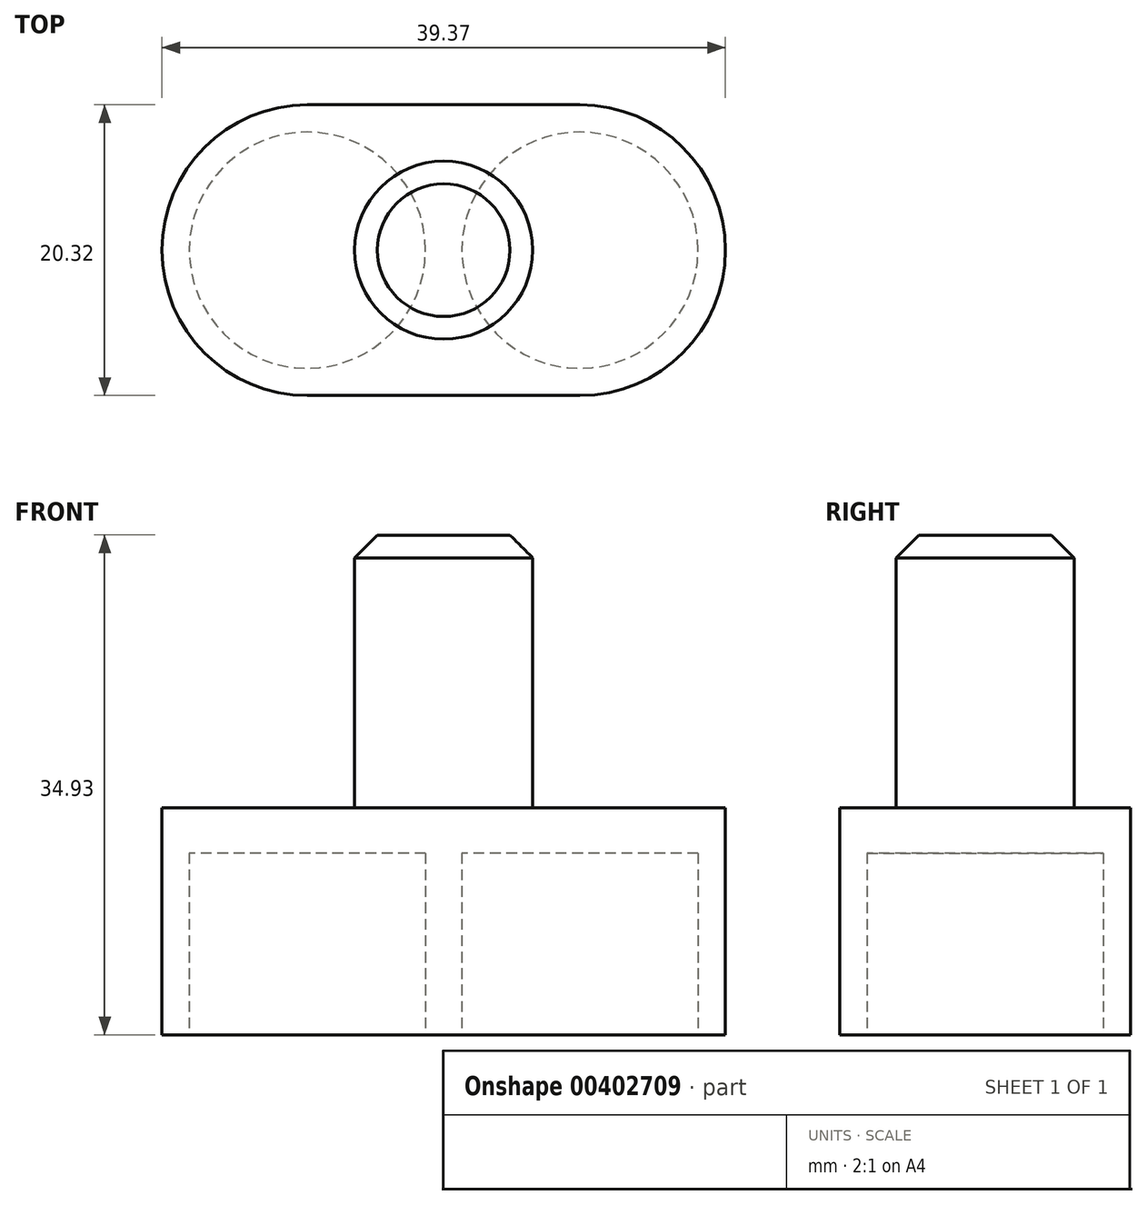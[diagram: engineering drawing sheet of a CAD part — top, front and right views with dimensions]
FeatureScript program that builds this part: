
annotation { "Feature Type Name" : "Feature", "Feature Type Description" : "" }
export const myFeature = defineFeature(function(context is Context, id is Id, definition is map)
    precondition{}
    {
        {
            var Q0;
            Q0=qCreatedBy(makeId("Top.planeOp"),FACE);
            var sketch = newSketch(context, id + "F0", { "sketchPlane" : qUnion([Q0])});
            skCircle(sketch, "E0", {"center": v(0, 0) * mm, "radius": 8.26 * mm});
            skCircle(sketch, "E1", {"center": v(19.05, 0) * mm, "radius": 8.26 * mm});
            skArc(sketch, "E2", {"start": v(0, 10.16) * mm, "mid": v(-10.16, 0) * mm, "end": v(0, -10.16) * mm});
            skArc(sketch, "E3", {"start": v(19.05, -10.16) * mm, "mid": v(29.21, 0) * mm, "end": v(19.05, 10.16) * mm});
            skLineSegment(sketch, "E4", {"start": v(0, 10.16) * mm, "end": v(19.05, 10.16) * mm});
            skLineSegment(sketch, "E5", {"start": v(0, -10.16) * mm, "end": v(19.05, -10.16) * mm});
            skSolve(sketch);
        }
        {
            var Q0;
            Q0 = qSketchRegion(id + "F0", true);
            extrude(context, id + "F1", {"entities" : qUnion([Q0]), "depth" : 12.7 * mm, "offsetDistance" : 25.4 * mm});
        }
        {
            var Q0;
            Q0=makeQuery(id+"F1.opExtrude","CAP_FACE",FACE,{"disambiguationData":[OSD([sQuery(id+"F0.wireOp",EDGE,"E0"),sQuery(id+"F0.wireOp",EDGE,"E1"),sQuery(id+"F0.wireOp",EDGE,"E2"),sQuery(id+"F0.wireOp",EDGE,"E3"),sQuery(id+"F0.wireOp",EDGE,"E4"),sQuery(id+"F0.wireOp",EDGE,"E5")])],"isStart":false});
            var sketch = newSketch(context, id + "F2", { "sketchPlane" : qUnion([Q0])});
            skLineSegment(sketch, "E6", {"start": v(0, 10.16) * mm, "end": v(19.05, 10.16) * mm});
            skArc(sketch, "E7", {"start": v(19.05, 10.16) * mm, "mid": v(29.21, 0) * mm, "end": v(19.05, -10.16) * mm});
            skLineSegment(sketch, "E8", {"start": v(19.05, -10.16) * mm, "end": v(0, -10.16) * mm});
            skArc(sketch, "E9", {"start": v(0, -10.16) * mm, "mid": v(-10.16, 0) * mm, "end": v(0, 10.16) * mm});
            skSolve(sketch);
        }
        {
            var Q0;
            Q0 = qSketchRegion(id + "F2", true);
            extrude(context, id + "F3", {"entities" : qUnion([Q0]), "operationType" : NewBodyOperationType.ADD, "depth" : 3.17 * mm, "offsetDistance" : 25.4 * mm});
        }
        {
            var Q0;
            Q0=makeQuery(id+"F3.opExtrude","CAP_FACE",FACE,{"disambiguationData":[OSD([sQuery(id+"F2.wireOp",EDGE,"E6"),sQuery(id+"F2.wireOp",EDGE,"E7"),sQuery(id+"F2.wireOp",EDGE,"E8"),sQuery(id+"F2.wireOp",EDGE,"E9")])],"isStart":false});
            var sketch = newSketch(context, id + "F4", { "sketchPlane" : qUnion([Q0])});
            skCircle(sketch, "E10", {"center": v(9.52, 0) * mm, "radius": 6.22 * mm});
            skPoint(sketch, "E10.centerSnap0", {"position": v(9.53, -10.16) * mm});
            skPoint(sketch, "E10.centerSnap1", {"position": v(-10.16, 0) * mm});
            skSolve(sketch);
        }
        {
            var Q0;
            Q0 = qSketchRegion(id + "F4", true);
            extrude(context, id + "F5", {"entities" : qUnion([Q0]), "operationType" : NewBodyOperationType.ADD, "depth" : 19.05 * mm, "offsetDistance" : 25.4 * mm});
        }
        {
            var Q0;
            Q0=makeQuery(id+"F5.opExtrude","CAP_EDGE",EDGE,{"disambiguationData":[OSD([sQuery(id+"F4.wireOp",EDGE,"E10")])],"isStart":false});
            chamfer(context, id + "F6", {"entities" : qUnion([Q0]), "width" : 1.59 * mm, "tangentPropagation" : true});
        }
    });
